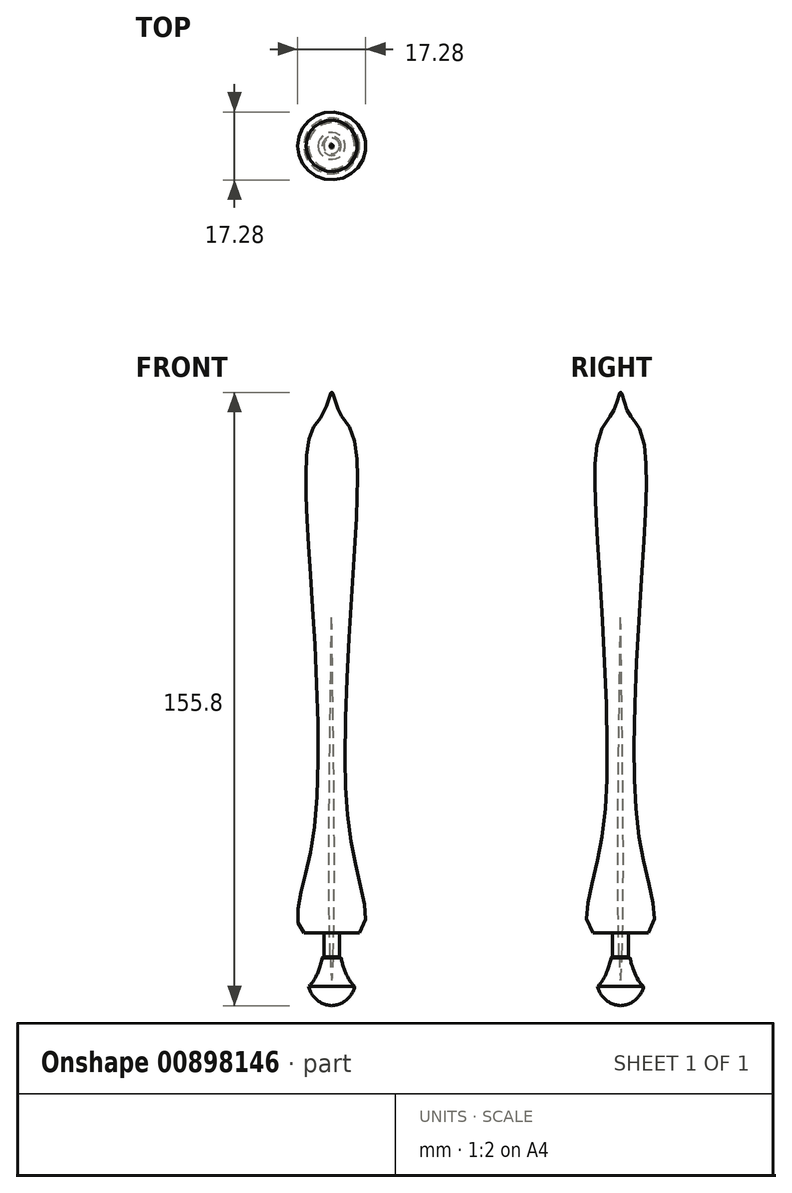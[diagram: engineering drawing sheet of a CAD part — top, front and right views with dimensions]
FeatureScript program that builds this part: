
annotation { "Feature Type Name" : "Feature", "Feature Type Description" : "" }
export const myFeature = defineFeature(function(context is Context, id is Id, definition is map)
    precondition{}
    {
        {
            var Q0;
            Q0=qCreatedBy(makeId("Right.planeOp"),FACE);
            var sketch = newSketch(context, id + "F0", { "sketchPlane" : qUnion([Q0])});
            skCircle(sketch, "E0", {"center": v(26.75, -6.17) * mm, "radius": 6.42 * mm});
            skLineSegment(sketch, "E1", {"start": v(29.13, -0.2) * mm, "end": v(29.13, 5.9) * mm});
            skLineSegment(sketch, "E2", {"start": v(29.13, 5.9) * mm, "end": v(35.44, 5.9) * mm});
            skLineSegment(sketch, "E3", {"start": v(27.13, 0.24) * mm, "end": v(27.13, -18.21) * mm});
            skLineSegment(sketch, "E4", {"start": v(27.6, 142.57) * mm, "end": v(25.86, 146.43) * mm});
            skLineSegment(sketch, "E5", {"start": v(25.86, 146.43) * mm, "end": v(24.71, 140.12) * mm});
            skLineSegment(sketch, "E6", {"start": v(24.71, 140.12) * mm, "end": v(27.65, 140.12) * mm});
            skFitSpline(sketch, "E7.trimOffspring", {"points": [v(27.13, 143.13) * mm, v(28.79, 138.85) * mm, v(32.04, 133.8) * mm, v(33.66, 121.77) * mm, v(32.21, 92.51) * mm, v(31.28, 34.48) * mm, v(35.3, 14.1) * mm, v(34.64, 6.29) * mm, v(29.94, 3.23) * mm, v(30.3, -3.22) * mm, v(32.48, -7.21) * mm, v(34.1, -9.33) * mm, v(32.33, -14.21) * mm, v(27.13, -13.79) * mm, v(27.13, -6.17) * mm, v(27.13, 143.13) * mm]});
            skLineSegment(sketch, "E8", {"start": v(27.13, 0.24) * mm, "end": v(27.13, 195.1) * mm});
            skSolve(sketch);
        }
        {
            var Q0;
            {var subQ5=sQuery(id+"F0.wireOp",EDGE,"E1");Q0=makeQuery(id+"F0.imprint","IMPRINT",FACE,{"disambiguationData":[TD([[makeQuery(id+"F0.imprint","IMPRINT",EDGE,{"derivedFrom":subQ5}),1.0]])]});}
            var Q1;
            {var subQ0=sQuery(id+"F0.wireOp",EDGE,"E0");var subQ1=makeQuery(id+"F0.imprint","INTERSECT",VERTEX,{"derivedFrom":[subQ0,sQuery(id+"F0.wireOp",EDGE,"E1")]});Q1=makeQuery(id+"F0.imprint","IMPRINT",FACE,{"disambiguationData":[TD([[makeQuery(id+"F0.imprint","IMPRINT",EDGE,{"disambiguationData":[TD([[subQ1,1.0]])],"derivedFrom":subQ0}),1.0]])]});}
            var Q2;
            Q2=sQuery(id+"F0.wireOp",EDGE,"E8");
            revolve(context, id + "F1", {"surfaceOperationType" : NewSurfaceOperationType.NEW, "entities" : qUnion([Q0, Q1]), "axis" : qUnion([Q2]), "revolveType" : RevolveType.FULL});
        }
    });
